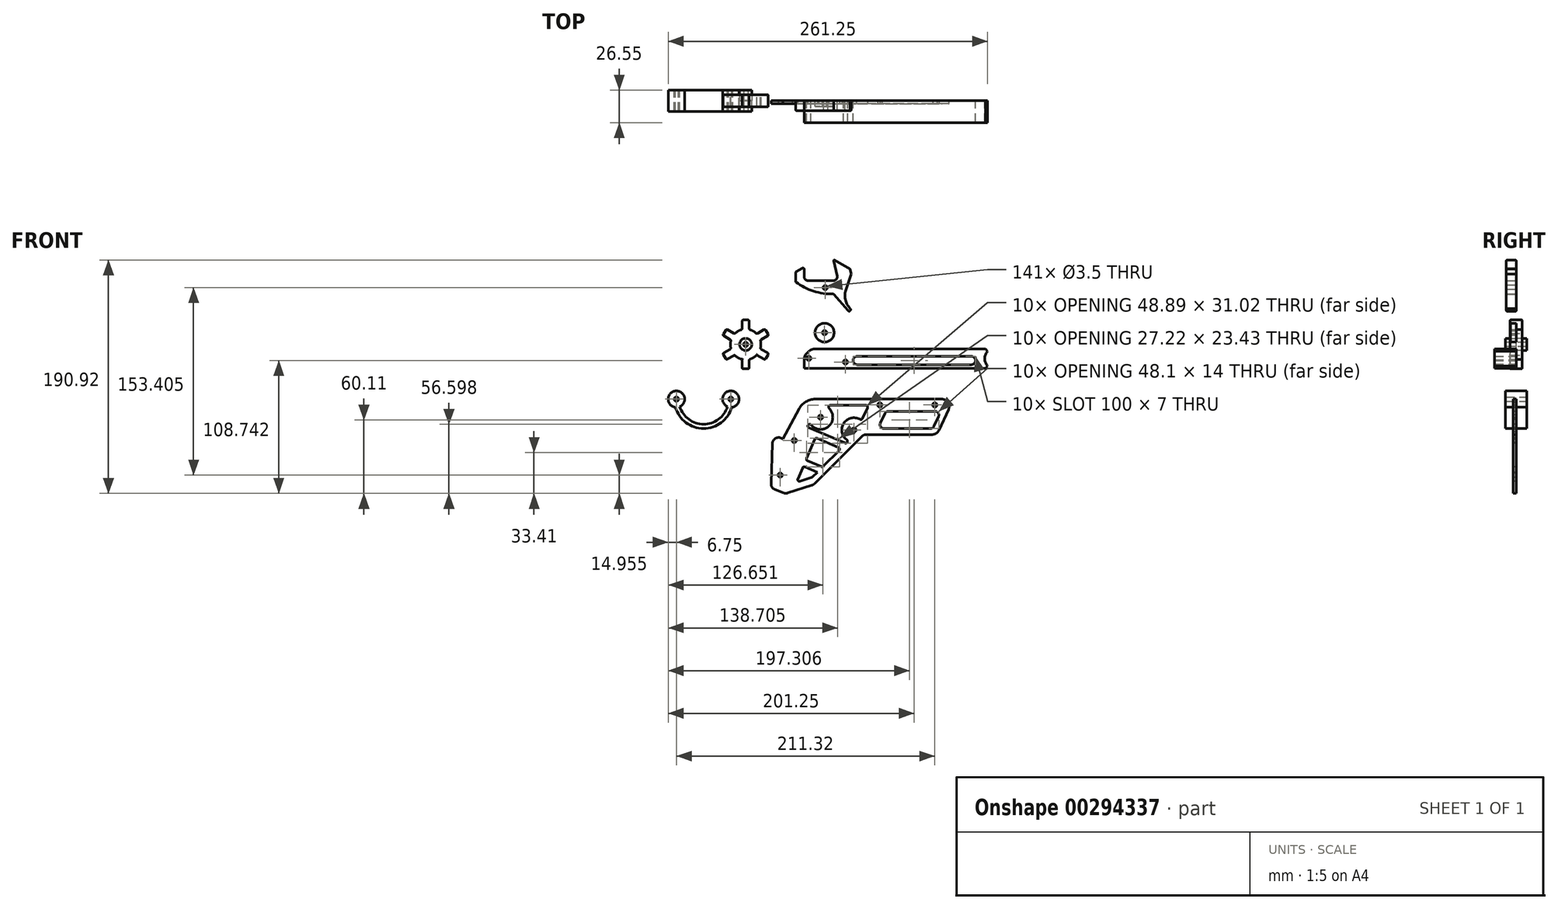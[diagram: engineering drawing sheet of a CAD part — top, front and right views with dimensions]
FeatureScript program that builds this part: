
annotation { "Feature Type Name" : "Feature", "Feature Type Description" : "" }
export const myFeature = defineFeature(function(context is Context, id is Id, definition is map)
    precondition{}
    {
        {
            var Q0;
            Q0=qCreatedBy(makeId("Front.planeOp"),FACE);
            var sketch = newSketch(context, id + "F0", { "sketchPlane" : qUnion([Q0])});
            skLineSegment(sketch, "E0", {"start": v(9.01, 0) * mm, "end": v(112.58, 0) * mm});
            skLineSegment(sketch, "E1", {"start": v(118.02, -8.54) * mm, "end": v(110.1, -25.54) * mm});
            skLineSegment(sketch, "E2", {"start": v(104.65, -29) * mm, "end": v(50.73, -29) * mm});
            skLineSegment(sketch, "E3", {"start": v(-4.23, -7.96) * mm, "end": v(-17.37, -32.67) * mm});
            skPoint(sketch, "E4.visualSharp", {"position": v(0, 0) * mm});
            skArc(sketch, "E4.filletArc", {"start": v(9.01, 0) * mm, "mid": v(1.29, -2.14) * mm, "end": v(-4.23, -7.96) * mm});
            skPoint(sketch, "E5.visualSharp", {"position": v(122, 0) * mm});
            skArc(sketch, "E5.filletArc", {"start": v(118.02, -8.54) * mm, "mid": v(117.64, -2.78) * mm, "end": v(112.58, 0) * mm});
            skPoint(sketch, "E6.visualSharp", {"position": v(108.48, -29) * mm});
            skArc(sketch, "E6.filletArc", {"start": v(104.65, -29) * mm, "mid": v(107.88, -28.06) * mm, "end": v(110.1, -25.54) * mm});
            skLineSegment(sketch, "E7", {"start": v(47.2, -30.46) * mm, "end": v(8.5, -69.16) * mm});
            skLineSegment(sketch, "E8", {"start": v(6.5, -70.38) * mm, "end": v(-13.45, -76.87) * mm});
            skLineSegment(sketch, "E9", {"start": v(-16.87, -76.75) * mm, "end": v(-24, -73.87) * mm});
            skLineSegment(sketch, "E10", {"start": v(-27.11, -69.06) * mm, "end": v(-25.97, -36.24) * mm});
            skCircle(sketch, "E11", {"center": v(-20.97, -36.42) * mm, "radius": 5 * mm});
            skLineSegment(sketch, "E12", {"start": v(-17.37, -32.67) * mm, "end": v(-18.62, -32) * mm});
            skPoint(sketch, "E13.visualSharp", {"position": v(48.65, -29) * mm});
            skArc(sketch, "E13.filletArc", {"start": v(50.73, -29) * mm, "mid": v(48.81, -29.38) * mm, "end": v(47.2, -30.46) * mm});
            skPoint(sketch, "E14.visualSharp", {"position": v(7.64, -70.01) * mm});
            skArc(sketch, "E14.filletArc", {"start": v(6.5, -70.38) * mm, "mid": v(7.57, -69.9) * mm, "end": v(8.5, -69.16) * mm});
            skPoint(sketch, "E15.visualSharp", {"position": v(-15.18, -77.43) * mm});
            skArc(sketch, "E15.filletArc", {"start": v(-16.87, -76.75) * mm, "mid": v(-15.17, -77.1) * mm, "end": v(-13.45, -76.87) * mm});
            skPoint(sketch, "E16.visualSharp", {"position": v(-27.24, -72.56) * mm});
            skArc(sketch, "E16.filletArc", {"start": v(-27.11, -69.06) * mm, "mid": v(-26.31, -71.96) * mm, "end": v(-24, -73.87) * mm});
            skSolve(sketch);
        }
        {
            var Q0;
            Q0=makeQuery(id+"F0.imprint","IMPRINT",FACE,{"disambiguationData":[TD([[makeQuery(id+"F0.imprint","IMPRINT",EDGE,{"derivedFrom":sQuery(id+"F0.wireOp",EDGE,"E0")}),-1.0]])]});
            var Q1;
            {var subQ0=sQuery(id+"F0.wireOp",EDGE,"E11");var subQ1=makeQuery(id+"F0.imprint","INTERSECT",VERTEX,{"derivedFrom":[sQuery(id+"F0.wireOp",EDGE,"E10"),subQ0]});Q1=makeQuery(id+"F0.imprint","IMPRINT",FACE,{"disambiguationData":[TD([[makeQuery(id+"F0.imprint","IMPRINT",EDGE,{"disambiguationData":[TD([[subQ1,1.0]])],"derivedFrom":subQ0}),1.0]])]});}
            extrude(context, id + "F1", {"entities" : qUnion([Q0, Q1]), "depth" : 2.5 * mm});
        }
        {
            var Q0;
            Q0=makeQuery(id+"F1.opExtrude","CAP_FACE",FACE,{"disambiguationData":[OSD([sQuery(id+"F0.wireOp",EDGE,"E0"),sQuery(id+"F0.wireOp",EDGE,"E1"),sQuery(id+"F0.wireOp",EDGE,"E2"),sQuery(id+"F0.wireOp",EDGE,"E3"),sQuery(id+"F0.wireOp",EDGE,"E4.filletArc"),sQuery(id+"F0.wireOp",EDGE,"E5.filletArc"),sQuery(id+"F0.wireOp",EDGE,"E6.filletArc"),sQuery(id+"F0.wireOp",EDGE,"E7"),sQuery(id+"F0.wireOp",EDGE,"E8"),sQuery(id+"F0.wireOp",EDGE,"E9"),sQuery(id+"F0.wireOp",EDGE,"E10"),sQuery(id+"F0.wireOp",EDGE,"E11"),sQuery(id+"F0.wireOp",EDGE,"E12"),sQuery(id+"F0.wireOp",EDGE,"E13.filletArc"),sQuery(id+"F0.wireOp",EDGE,"E14.filletArc"),sQuery(id+"F0.wireOp",EDGE,"E15.filletArc"),sQuery(id+"F0.wireOp",EDGE,"E16.filletArc")])],"isStart":false});
            var sketch = newSketch(context, id + "F2", { "sketchPlane" : qUnion([Q0])});
            skLineSegment(sketch, "E17.0", {"start": v(103.38, -24) * mm, "end": v(65, -24) * mm});
            skLineSegment(sketch, "E17.2", {"start": v(109.83, -14.27) * mm, "end": v(106.1, -22.27) * mm});
            skLineSegment(sketch, "E18.1", {"start": v(68.73, -10) * mm, "end": v(107.11, -10) * mm});
            skLineSegment(sketch, "E19", {"start": v(66.01, -11.73) * mm, "end": v(62.28, -19.73) * mm});
            skPoint(sketch, "E20.visualSharp", {"position": v(111.82, -10) * mm});
            skArc(sketch, "E20.filletArc", {"start": v(109.83, -14.27) * mm, "mid": v(109.64, -11.39) * mm, "end": v(107.11, -10) * mm});
            skPoint(sketch, "E21.visualSharp", {"position": v(105.3, -24) * mm});
            skArc(sketch, "E21.filletArc", {"start": v(103.38, -24) * mm, "mid": v(105, -23.53) * mm, "end": v(106.1, -22.27) * mm});
            skPoint(sketch, "E22.visualSharp", {"position": v(66.82, -10) * mm});
            skArc(sketch, "E22.filletArc", {"start": v(68.73, -10) * mm, "mid": v(67.12, -10.47) * mm, "end": v(66.01, -11.73) * mm});
            skPoint(sketch, "E23.visualSharp", {"position": v(60.3, -24) * mm});
            skArc(sketch, "E23.filletArc", {"start": v(62.28, -19.73) * mm, "mid": v(62.47, -22.61) * mm, "end": v(65, -24) * mm});
            skCircle(sketch, "E24", {"center": v(106.82, -4.75) * mm, "radius": 1.75 * mm});
            skCircle(sketch, "E25", {"center": v(61.82, -4.75) * mm, "radius": 1.75 * mm});
            skCircle(sketch, "E26", {"center": v(40.74, -25.25) * mm, "radius": 1.75 * mm});
            skCircle(sketch, "E27", {"center": v(13.4, -14.75) * mm, "radius": 1.75 * mm});
            skCircle(sketch, "E28", {"center": v(-19.62, -62.15) * mm, "radius": 1.75 * mm});
            skCircle(sketch, "E29", {"center": v(-8.1, -33.85) * mm, "radius": 1.75 * mm});
            skLineSegment(sketch, "E30", {"start": v(21.4, -5) * mm, "end": v(50.4, -5) * mm});
            skCircle(sketch, "E31", {"center": v(50.4, -6.5) * mm, "radius": 1.5 * mm});
            skCircle(sketch, "E32", {"center": v(21.4, -6.5) * mm, "radius": 1.5 * mm});
            skLineSegment(sketch, "E33", {"start": v(-6.47, -68.29) * mm, "end": v(6.51, -64.07) * mm});
            skLineSegment(sketch, "E34", {"start": v(6.51, -64.07) * mm, "end": v(10.76, -59.83) * mm});
            skLineSegment(sketch, "E35", {"start": v(-0.8, -54.92) * mm, "end": v(-6.47, -68.29) * mm});
            skCircle(sketch, "E36", {"center": v(-3.8, -65.85) * mm, "radius": 1.5 * mm});
            skCircle(sketch, "E37", {"center": v(8.12, -60.34) * mm, "radius": 1.5 * mm});
            skCircle(sketch, "E38", {"center": v(5.7, -62.76) * mm, "radius": 1.5 * mm});
            skCircle(sketch, "E39", {"center": v(3.3, -49.14) * mm, "radius": 1.5 * mm});
            skCircle(sketch, "E40", {"center": v(9.93, -33.49) * mm, "radius": 1.5 * mm});
            skCircle(sketch, "E41", {"center": v(27.51, -40.95) * mm, "radius": 1.5 * mm});
            skCircle(sketch, "E42", {"center": v(14.55, -53.91) * mm, "radius": 1.5 * mm});
            skLineSegment(sketch, "E43", {"start": v(26.92, -74.55) * mm, "end": v(36.43, -74.55) * mm});
            skLineSegment(sketch, "E44", {"start": v(-0.8, -54.92) * mm, "end": v(10.76, -59.83) * mm});
            skCircle(sketch, "E45", {"center": v(0, -56.9) * mm, "radius": 1.5 * mm});
            skLineSegment(sketch, "E46", {"start": v(1.32, -49.93) * mm, "end": v(14.9, -55.7) * mm});
            skLineSegment(sketch, "E47", {"start": v(-0.8, -54.92) * mm, "end": v(9.14, -31.52) * mm});
            skLineSegment(sketch, "E48", {"start": v(9.14, -31.52) * mm, "end": v(30.15, -40.44) * mm});
            skLineSegment(sketch, "E49", {"start": v(19.38, -58.28) * mm, "end": v(22.63, -55.02) * mm});
            skLineSegment(sketch, "E50", {"start": v(10.76, -59.83) * mm, "end": v(30.15, -40.44) * mm});
            skCircle(sketch, "E51", {"center": v(13.4, -14.75) * mm, "radius": 10 * mm});
            skCircle(sketch, "E52", {"center": v(40.74, -25.25) * mm, "radius": 10 * mm});
            skCircle(sketch, "E53", {"center": v(4.48, -22.02) * mm, "radius": 1.5 * mm});
            skCircle(sketch, "E54", {"center": v(33.94, -34.52) * mm, "radius": 1.5 * mm});
            skLineSegment(sketch, "E55", {"start": v(3.9, -23.4) * mm, "end": v(33.35, -35.9) * mm});
            skLineSegment(sketch, "E56", {"start": v(30.15, -40.44) * mm, "end": v(35, -35.59) * mm});
            skLineSegment(sketch, "E57", {"start": v(14.9, -55.7) * mm, "end": v(10.76, -59.83) * mm});
            skLineSegment(sketch, "E58", {"start": v(9.14, -31.52) * mm, "end": v(11.26, -26.53) * mm});
            skLineSegment(sketch, "E59", {"start": v(1.87, -56.05) * mm, "end": v(3.99, -51.06) * mm});
            skCircle(sketch, "E60", {"center": v(46.34, -15.2) * mm, "radius": 1.5 * mm});
            skLineSegment(sketch, "E61", {"start": v(47.7, -15.84) * mm, "end": v(51.76, -7.13) * mm});
            skSolve(sketch);
        }
        {
            var Q0;
            {var subQ13=sQuery(id+"F2.wireOp",EDGE,"E30");Q0=makeQuery(id+"F2.imprint","IMPRINT",FACE,{"disambiguationData":[TD([[makeQuery(id+"F2.imprint","IMPRINT",EDGE,{"derivedFrom":subQ13}),-1.0]])]});}
            var Q1;
            {var subQ0=sQuery(id+"F2.wireOp",EDGE,"E53");var subQ1=makeQuery(id+"F2.imprint","INTERSECT",VERTEX,{"derivedFrom":[subQ0,sQuery(id+"F2.wireOp",EDGE,"E55")]});Q1=makeQuery(id+"F2.imprint","IMPRINT",FACE,{"disambiguationData":[TD([[makeQuery(id+"F2.imprint","IMPRINT",EDGE,{"disambiguationData":[TD([[subQ1,1.0]])],"derivedFrom":subQ0}),1.0]])]});}
            var Q2;
            {var subQ0=sQuery(id+"F2.wireOp",EDGE,"E32");var subQ1=makeQuery(id+"F2.imprint","INTERSECT",VERTEX,{"derivedFrom":[sQuery(id+"F2.wireOp",EDGE,"E30"),subQ0]});Q2=makeQuery(id+"F2.imprint","IMPRINT",FACE,{"disambiguationData":[TD([[makeQuery(id+"F2.imprint","IMPRINT",EDGE,{"disambiguationData":[TD([[subQ1,-1.0]])],"derivedFrom":subQ0}),1.0]])]});}
            var Q3;
            {var subQ0=sQuery(id+"F2.wireOp",EDGE,"E31");var subQ1=makeQuery(id+"F2.imprint","INTERSECT",VERTEX,{"derivedFrom":[sQuery(id+"F2.wireOp",EDGE,"E30"),subQ0]});Q3=makeQuery(id+"F2.imprint","IMPRINT",FACE,{"disambiguationData":[TD([[makeQuery(id+"F2.imprint","IMPRINT",EDGE,{"disambiguationData":[TD([[subQ1,-1.0]])],"derivedFrom":subQ0}),1.0]])]});}
            var Q4;
            {var subQ0=sQuery(id+"F2.wireOp",EDGE,"E60");var subQ1=makeQuery(id+"F2.imprint","INTERSECT",VERTEX,{"derivedFrom":[subQ0,sQuery(id+"F2.wireOp",EDGE,"E61")]});Q4=makeQuery(id+"F2.imprint","IMPRINT",FACE,{"disambiguationData":[TD([[makeQuery(id+"F2.imprint","IMPRINT",EDGE,{"disambiguationData":[TD([[subQ1,1.0]])],"derivedFrom":subQ0}),1.0]])]});}
            var Q5;
            Q5=makeQuery(id+"F2.imprint","IMPRINT",FACE,{"disambiguationData":[TD([[makeQuery(id+"F2.imprint","IMPRINT",EDGE,{"derivedFrom":sQuery(id+"F2.wireOp",EDGE,"E17.0")}),-1.0]])]});
            var Q6;
            {var subQ0=sQuery(id+"F2.wireOp",EDGE,"E46");var subQ10=sQuery(id+"F2.wireOp",EDGE,"E39");var subQ11=makeQuery(id+"F2.imprint","INTERSECT",VERTEX,{"derivedFrom":[subQ10,subQ0]});Q6=makeQuery(id+"F2.imprint","IMPRINT",FACE,{"disambiguationData":[TD([[makeQuery(id+"F2.imprint","IMPRINT",EDGE,{"disambiguationData":[TD([[subQ11,-1.0]])],"derivedFrom":subQ10}),-1.0]])]});}
            var Q7;
            {var subQ0=sQuery(id+"F2.wireOp",EDGE,"E40");var subQ1=makeQuery(id+"F2.imprint","INTERSECT",VERTEX,{"derivedFrom":[subQ0,sQuery(id+"F2.wireOp",EDGE,"E47")]});Q7=makeQuery(id+"F2.imprint","IMPRINT",FACE,{"disambiguationData":[TD([[makeQuery(id+"F2.imprint","IMPRINT",EDGE,{"disambiguationData":[TD([[subQ1,1.0]])],"derivedFrom":subQ0}),1.0]])]});}
            var Q8;
            {var subQ0=sQuery(id+"F2.wireOp",EDGE,"E39");var subQ1=makeQuery(id+"F2.imprint","INTERSECT",VERTEX,{"derivedFrom":[subQ0,sQuery(id+"F2.wireOp",EDGE,"E46")]});Q8=makeQuery(id+"F2.imprint","IMPRINT",FACE,{"disambiguationData":[TD([[makeQuery(id+"F2.imprint","IMPRINT",EDGE,{"disambiguationData":[TD([[subQ1,1.0]])],"derivedFrom":subQ0}),1.0]])]});}
            var Q9;
            {var subQ0=sQuery(id+"F2.wireOp",EDGE,"E42");var subQ1=makeQuery(id+"F2.imprint","INTERSECT",VERTEX,{"derivedFrom":[subQ0,sQuery(id+"F2.wireOp",EDGE,"E46")]});Q9=makeQuery(id+"F2.imprint","IMPRINT",FACE,{"disambiguationData":[TD([[makeQuery(id+"F2.imprint","IMPRINT",EDGE,{"disambiguationData":[TD([[subQ1,-1.0]])],"derivedFrom":subQ0}),1.0]])]});}
            var Q10;
            {var subQ0=sQuery(id+"F2.wireOp",EDGE,"E41");var subQ1=makeQuery(id+"F2.imprint","INTERSECT",VERTEX,{"derivedFrom":[subQ0,sQuery(id+"F2.wireOp",EDGE,"E48")]});Q10=makeQuery(id+"F2.imprint","IMPRINT",FACE,{"disambiguationData":[TD([[makeQuery(id+"F2.imprint","IMPRINT",EDGE,{"disambiguationData":[TD([[subQ1,-1.0]])],"derivedFrom":subQ0}),1.0]])]});}
            var Q11;
            {var subQ0=sQuery(id+"F2.wireOp",EDGE,"E36");var subQ1=sQuery(id+"F2.wireOp",EDGE,"E33");var subQ2=makeQuery(id+"F2.imprint","INTERSECT",VERTEX,{"derivedFrom":[subQ1,subQ0]});Q11=makeQuery(id+"F2.imprint","IMPRINT",FACE,{"disambiguationData":[TD([[makeQuery(id+"F2.imprint","IMPRINT",EDGE,{"disambiguationData":[TD([[subQ2,-1.0]])],"derivedFrom":subQ1}),1.0]])]});}
            var Q12;
            {var subQ0=sQuery(id+"F2.wireOp",EDGE,"E38");var subQ1=sQuery(id+"F2.wireOp",EDGE,"E37");var subQ2=makeQuery(id+"F2.imprint","INTERSECT",VERTEX,{"disambiguationData":[OD(0.0)],"derivedFrom":[subQ1,subQ0]});Q12=makeQuery(id+"F2.imprint","IMPRINT",FACE,{"disambiguationData":[TD([[makeQuery(id+"F2.imprint","IMPRINT",EDGE,{"disambiguationData":[TD([[subQ2,1.0]])],"derivedFrom":subQ1}),1.0]])]});}
            var Q13;
            {var subQ0=sQuery(id+"F2.wireOp",EDGE,"E36");var subQ1=makeQuery(id+"F2.imprint","INTERSECT",VERTEX,{"derivedFrom":[sQuery(id+"F2.wireOp",EDGE,"E33"),subQ0]});Q13=makeQuery(id+"F2.imprint","IMPRINT",FACE,{"disambiguationData":[TD([[makeQuery(id+"F2.imprint","IMPRINT",EDGE,{"disambiguationData":[TD([[subQ1,1.0]])],"derivedFrom":subQ0}),1.0]])]});}
            var Q14;
            {var subQ0=sQuery(id+"F2.wireOp",EDGE,"E45");var subQ1=makeQuery(id+"F2.imprint","INTERSECT",VERTEX,{"derivedFrom":[sQuery(id+"F2.wireOp",EDGE,"E35"),subQ0]});Q14=makeQuery(id+"F2.imprint","IMPRINT",FACE,{"disambiguationData":[TD([[makeQuery(id+"F2.imprint","IMPRINT",EDGE,{"disambiguationData":[TD([[subQ1,1.0]])],"derivedFrom":subQ0}),1.0]])]});}
            var Q15;
            {var subQ0=sQuery(id+"F2.wireOp",EDGE,"E38");var subQ1=sQuery(id+"F2.wireOp",EDGE,"E37");var subQ2=makeQuery(id+"F2.imprint","INTERSECT",VERTEX,{"disambiguationData":[OD(0.0)],"derivedFrom":[subQ1,subQ0]});Q15=makeQuery(id+"F2.imprint","IMPRINT",FACE,{"disambiguationData":[TD([[makeQuery(id+"F2.imprint","IMPRINT",EDGE,{"disambiguationData":[TD([[subQ2,-1.0]])],"derivedFrom":subQ1}),1.0]])]});}
            var Q16;
            {var subQ0=sQuery(id+"F2.wireOp",EDGE,"E38");var subQ1=sQuery(id+"F2.wireOp",EDGE,"E37");var subQ2=makeQuery(id+"F2.imprint","INTERSECT",VERTEX,{"disambiguationData":[OD(0.0)],"derivedFrom":[subQ1,subQ0]});Q16=makeQuery(id+"F2.imprint","IMPRINT",FACE,{"disambiguationData":[TD([[makeQuery(id+"F2.imprint","IMPRINT",EDGE,{"disambiguationData":[TD([[subQ2,-1.0]])],"derivedFrom":subQ1}),-1.0]])]});}
            var Q17;
            {var subQ0=sQuery(id+"F2.wireOp",EDGE,"E38");var subQ1=sQuery(id+"F2.wireOp",EDGE,"E34");var subQ2=makeQuery(id+"F2.imprint","INTERSECT",VERTEX,{"derivedFrom":[subQ1,subQ0]});Q17=makeQuery(id+"F2.imprint","IMPRINT",FACE,{"disambiguationData":[TD([[makeQuery(id+"F2.imprint","IMPRINT",EDGE,{"disambiguationData":[TD([[subQ2,-1.0]])],"derivedFrom":subQ1}),1.0]])]});}
            var Q18;
            Q18=makeQuery(id+"F2.imprint","IMPRINT",FACE,{"disambiguationData":[TD([[makeQuery(id+"F2.imprint","IMPRINT",EDGE,{"derivedFrom":sQuery(id+"F2.wireOp",EDGE,"E28")}),1.0]])]});
            var Q19;
            Q19=makeQuery(id+"F2.imprint","IMPRINT",FACE,{"disambiguationData":[TD([[makeQuery(id+"F2.imprint","IMPRINT",EDGE,{"derivedFrom":sQuery(id+"F2.wireOp",EDGE,"E29")}),1.0]])]});
            var Q20;
            {var subQ0=sQuery(id+"F2.wireOp",EDGE,"E54");var subQ1=makeQuery(id+"F2.imprint","INTERSECT",VERTEX,{"derivedFrom":[subQ0,sQuery(id+"F2.wireOp",EDGE,"E55")]});Q20=makeQuery(id+"F2.imprint","IMPRINT",FACE,{"disambiguationData":[TD([[makeQuery(id+"F2.imprint","IMPRINT",EDGE,{"disambiguationData":[TD([[subQ1,1.0]])],"derivedFrom":subQ0}),1.0]])]});}
            var Q21;
            Q21=makeQuery(id+"F2.imprint","IMPRINT",FACE,{"disambiguationData":[TD([[makeQuery(id+"F2.imprint","IMPRINT",EDGE,{"derivedFrom":sQuery(id+"F2.wireOp",EDGE,"E27")}),1.0]])]});
            var Q22;
            Q22=makeQuery(id+"F2.imprint","IMPRINT",FACE,{"disambiguationData":[TD([[makeQuery(id+"F2.imprint","IMPRINT",EDGE,{"derivedFrom":sQuery(id+"F2.wireOp",EDGE,"E26")}),1.0]])]});
            var Q23;
            Q23=makeQuery(id+"F2.imprint","IMPRINT",FACE,{"disambiguationData":[TD([[makeQuery(id+"F2.imprint","IMPRINT",EDGE,{"derivedFrom":sQuery(id+"F2.wireOp",EDGE,"E25")}),1.0]])]});
            var Q24;
            Q24=makeQuery(id+"F2.imprint","IMPRINT",FACE,{"disambiguationData":[TD([[makeQuery(id+"F2.imprint","IMPRINT",EDGE,{"derivedFrom":sQuery(id+"F2.wireOp",EDGE,"E24")}),1.0]])]});
            var Q25;
            {var subQ0=sQuery(id+"F2.wireOp",EDGE,"E38");var subQ1=makeQuery(id+"F2.imprint","INTERSECT",VERTEX,{"derivedFrom":[sQuery(id+"F2.wireOp",EDGE,"E33"),subQ0]});Q25=makeQuery(id+"F2.imprint","IMPRINT",FACE,{"disambiguationData":[TD([[makeQuery(id+"F2.imprint","IMPRINT",EDGE,{"disambiguationData":[TD([[subQ1,-1.0]])],"derivedFrom":subQ0}),1.0]])]});}
            extrude(context, id + "F3", {"entities" : qUnion([Q0, Q1, Q2, Q3, Q4, Q5, Q6, Q7, Q8, Q9, Q10, Q11, Q12, Q13, Q14, Q15, Q16, Q17, Q18, Q19, Q20, Q21, Q22, Q23, Q24, Q25]), "operationType" : NewBodyOperationType.REMOVE, "endBound" : BoundingType.THROUGH_ALL, "oppositeDirection" : true, "depth" : 25 * mm});
        }
        {
            var Q0;
            Q0=qCreatedBy(makeId("Front.planeOp"),FACE);
            var sketch = newSketch(context, id + "F4", { "sketchPlane" : qUnion([Q0])});
            skCircle(sketch, "E62", {"center": v(-47.87, 44.76) * mm, "radius": 12.5 * mm});
            skLineSegment(sketch, "E63", {"start": v(-50.8, 56.91) * mm, "end": v(-50.8, 64.76) * mm});
            skLineSegment(sketch, "E64", {"start": v(-50.8, 64.76) * mm, "end": v(-44.93, 64.76) * mm});
            skLineSegment(sketch, "E65", {"start": v(-44.93, 64.76) * mm, "end": v(-44.93, 56.91) * mm});
            skLineSegment(sketch, "E66", {"start": v(-47.87, 64.76) * mm, "end": v(-47.87, 44.76) * mm});
            skLineSegment(sketch, "E67.1.0", {"start": v(-66.66, 52.22) * mm, "end": v(-63.72, 57.3) * mm});
            skLineSegment(sketch, "E67.1.1", {"start": v(-63.72, 57.3) * mm, "end": v(-56.92, 53.38) * mm});
            skLineSegment(sketch, "E67.1.2", {"start": v(-59.86, 48.3) * mm, "end": v(-66.66, 52.22) * mm});
            skLineSegment(sketch, "E67.2.0", {"start": v(-63.72, 32.22) * mm, "end": v(-66.66, 37.3) * mm});
            skLineSegment(sketch, "E67.2.1", {"start": v(-66.66, 37.3) * mm, "end": v(-59.86, 41.23) * mm});
            skLineSegment(sketch, "E67.2.2", {"start": v(-56.92, 36.14) * mm, "end": v(-63.72, 32.22) * mm});
            skLineSegment(sketch, "E67.3.0", {"start": v(-44.93, 24.76) * mm, "end": v(-50.8, 24.76) * mm});
            skLineSegment(sketch, "E67.3.1", {"start": v(-50.8, 24.76) * mm, "end": v(-50.8, 32.61) * mm});
            skLineSegment(sketch, "E67.3.2", {"start": v(-44.93, 32.61) * mm, "end": v(-44.93, 24.76) * mm});
            skLineSegment(sketch, "E67.4.0", {"start": v(-29.08, 37.3) * mm, "end": v(-32.02, 32.22) * mm});
            skLineSegment(sketch, "E67.4.1", {"start": v(-32.02, 32.22) * mm, "end": v(-38.82, 36.14) * mm});
            skLineSegment(sketch, "E67.4.2", {"start": v(-35.88, 41.23) * mm, "end": v(-29.08, 37.3) * mm});
            skLineSegment(sketch, "E67.5.0", {"start": v(-32.02, 57.3) * mm, "end": v(-29.08, 52.22) * mm});
            skLineSegment(sketch, "E67.5.1", {"start": v(-29.08, 52.22) * mm, "end": v(-35.88, 48.3) * mm});
            skLineSegment(sketch, "E67.5.2", {"start": v(-38.82, 53.38) * mm, "end": v(-32.02, 57.3) * mm});
            skSolve(sketch);
        }
        {
            var Q0;
            Q0 = qSketchRegion(id + "F4", true);
            extrude(context, id + "F5", {"entities" : qUnion([Q0]), "endBound" : BoundingType.SYMMETRIC, "depth" : 10 * mm});
        }
        {
            var Q0;
            Q0=qCreatedBy(makeId("Front.planeOp"),FACE);
            var sketch = newSketch(context, id + "F6", { "sketchPlane" : qUnion([Q0])});
            skCircle(sketch, "E68", {"center": v(-47.87, 44.76) * mm, "radius": 5 * mm});
            skCircle(sketch, "E69", {"center": v(-47.87, 44.76) * mm, "radius": 12.5 * mm});
            skSolve(sketch);
        }
        {
            var Q0;
            Q0=makeQuery(id+"F6.imprint","IMPRINT",FACE,{"disambiguationData":[TD([[makeQuery(id+"F6.imprint","IMPRINT",EDGE,{"derivedFrom":sQuery(id+"F6.wireOp",EDGE,"E68")}),1.0]])]});
            var Q1;
            Q1 = qConstructionFilter(qBodyType(qCreatedBy(id + "F6" ,EDGE), BodyType.WIRE), ConstructionObject.NO);
            extrude(context, id + "F7", {"entities" : qUnion([Q0]), "surfaceEntities" : qUnion([Q1]), "depth" : 8.75 * mm});
        }
        {
            var Q0;
            Q0=makeQuery(id+"F6.imprint","IMPRINT",FACE,{"disambiguationData":[TD([[makeQuery(id+"F6.imprint","IMPRINT",EDGE,{"derivedFrom":sQuery(id+"F6.wireOp",EDGE,"E68")}),1.0]])]});
            extrude(context, id + "F8", {"entities" : qUnion([Q0]), "operationType" : NewBodyOperationType.REMOVE, "endBound" : BoundingType.THROUGH_ALL, "oppositeDirection" : true, "depth" : 25 * mm});
        }
        {
            var Q0;
            Q0=makeQuery(id+"F7.opExtrude","CAP_FACE",FACE,{"disambiguationData":[OSD([sQuery(id+"F6.wireOp",EDGE,"E68")])],"isStart":false});
            var sketch = newSketch(context, id + "F9", { "sketchPlane" : qUnion([Q0])});
            skCircle(sketch, "E70", {"center": v(-47.87, 44.76) * mm, "radius": 1.75 * mm});
            skSolve(sketch);
        }
        {
            var Q0;
            Q0=makeQuery(id+"F9.imprint","IMPRINT",FACE,{"disambiguationData":[TD([[makeQuery(id+"F9.imprint","IMPRINT",EDGE,{"derivedFrom":sQuery(id+"F9.wireOp",EDGE,"E70")}),1.0]])]});
            extrude(context, id + "F10", {"entities" : qUnion([Q0]), "operationType" : NewBodyOperationType.REMOVE, "endBound" : BoundingType.THROUGH_ALL, "oppositeDirection" : true, "depth" : 25 * mm});
        }
        {
            var Q0;
            Q0=makeQuery(id+"F5.opExtrude","SWEPT_EDGE",EDGE,{"disambiguationData":[OSD([sQuery(id+"F4.wireOp",EDGE,"E62"),sQuery(id+"F4.wireOp",EDGE,"E67.5.2")])]});
            var Q1;
            Q1=makeQuery(id+"F5.opExtrude","SWEPT_EDGE",EDGE,{"disambiguationData":[OSD([sQuery(id+"F4.wireOp",EDGE,"E62"),sQuery(id+"F4.wireOp",EDGE,"E65")])]});
            var Q2;
            Q2=makeQuery(id+"F5.opExtrude","SWEPT_EDGE",EDGE,{"disambiguationData":[OSD([sQuery(id+"F4.wireOp",EDGE,"E64"),sQuery(id+"F4.wireOp",EDGE,"E65")])]});
            var Q3;
            Q3=makeQuery(id+"F5.opExtrude","SWEPT_EDGE",EDGE,{"disambiguationData":[OSD([sQuery(id+"F4.wireOp",EDGE,"E63"),sQuery(id+"F4.wireOp",EDGE,"E64")])]});
            var Q4;
            Q4=makeQuery(id+"F5.opExtrude","SWEPT_EDGE",EDGE,{"disambiguationData":[OSD([sQuery(id+"F4.wireOp",EDGE,"E67.5.0"),sQuery(id+"F4.wireOp",EDGE,"E67.5.2")])]});
            var Q5;
            Q5=makeQuery(id+"F5.opExtrude","SWEPT_EDGE",EDGE,{"disambiguationData":[OSD([sQuery(id+"F4.wireOp",EDGE,"E67.5.0"),sQuery(id+"F4.wireOp",EDGE,"E67.5.1")])]});
            var Q6;
            Q6=makeQuery(id+"F5.opExtrude","SWEPT_EDGE",EDGE,{"disambiguationData":[OSD([sQuery(id+"F4.wireOp",EDGE,"E62"),sQuery(id+"F4.wireOp",EDGE,"E67.5.1")])]});
            var Q7;
            Q7=makeQuery(id+"F5.opExtrude","SWEPT_EDGE",EDGE,{"disambiguationData":[OSD([sQuery(id+"F4.wireOp",EDGE,"E62"),sQuery(id+"F4.wireOp",EDGE,"E67.4.2")])]});
            var Q8;
            Q8=makeQuery(id+"F5.opExtrude","SWEPT_EDGE",EDGE,{"disambiguationData":[OSD([sQuery(id+"F4.wireOp",EDGE,"E67.4.0"),sQuery(id+"F4.wireOp",EDGE,"E67.4.2")])]});
            var Q9;
            Q9=makeQuery(id+"F5.opExtrude","SWEPT_EDGE",EDGE,{"disambiguationData":[OSD([sQuery(id+"F4.wireOp",EDGE,"E67.4.0"),sQuery(id+"F4.wireOp",EDGE,"E67.4.1")])]});
            var Q10;
            Q10=makeQuery(id+"F5.opExtrude","SWEPT_EDGE",EDGE,{"disambiguationData":[OSD([sQuery(id+"F4.wireOp",EDGE,"E62"),sQuery(id+"F4.wireOp",EDGE,"E67.3.2")])]});
            var Q11;
            Q11=makeQuery(id+"F5.opExtrude","SWEPT_EDGE",EDGE,{"disambiguationData":[OSD([sQuery(id+"F4.wireOp",EDGE,"E67.3.0"),sQuery(id+"F4.wireOp",EDGE,"E67.3.2")])]});
            var Q12;
            Q12=makeQuery(id+"F5.opExtrude","SWEPT_EDGE",EDGE,{"disambiguationData":[OSD([sQuery(id+"F4.wireOp",EDGE,"E67.3.0"),sQuery(id+"F4.wireOp",EDGE,"E67.3.1")])]});
            var Q13;
            Q13=makeQuery(id+"F5.opExtrude","SWEPT_EDGE",EDGE,{"disambiguationData":[OSD([sQuery(id+"F4.wireOp",EDGE,"E62"),sQuery(id+"F4.wireOp",EDGE,"E67.2.2")])]});
            var Q14;
            Q14=makeQuery(id+"F5.opExtrude","SWEPT_EDGE",EDGE,{"disambiguationData":[OSD([sQuery(id+"F4.wireOp",EDGE,"E67.2.0"),sQuery(id+"F4.wireOp",EDGE,"E67.2.2")])]});
            var Q15;
            Q15=makeQuery(id+"F5.opExtrude","SWEPT_EDGE",EDGE,{"disambiguationData":[OSD([sQuery(id+"F4.wireOp",EDGE,"E67.2.0"),sQuery(id+"F4.wireOp",EDGE,"E67.2.1")])]});
            var Q16;
            Q16=makeQuery(id+"F5.opExtrude","SWEPT_EDGE",EDGE,{"disambiguationData":[OSD([sQuery(id+"F4.wireOp",EDGE,"E62"),sQuery(id+"F4.wireOp",EDGE,"E67.1.2")])]});
            var Q17;
            Q17=makeQuery(id+"F5.opExtrude","SWEPT_EDGE",EDGE,{"disambiguationData":[OSD([sQuery(id+"F4.wireOp",EDGE,"E67.1.0"),sQuery(id+"F4.wireOp",EDGE,"E67.1.2")])]});
            var Q18;
            Q18=makeQuery(id+"F5.opExtrude","SWEPT_EDGE",EDGE,{"disambiguationData":[OSD([sQuery(id+"F4.wireOp",EDGE,"E67.1.0"),sQuery(id+"F4.wireOp",EDGE,"E67.1.1")])]});
            var Q19;
            Q19=makeQuery(id+"F5.opExtrude","SWEPT_EDGE",EDGE,{"disambiguationData":[OSD([sQuery(id+"F4.wireOp",EDGE,"E62"),sQuery(id+"F4.wireOp",EDGE,"E67.1.1")])]});
            var Q20;
            Q20=makeQuery(id+"F5.opExtrude","SWEPT_EDGE",EDGE,{"disambiguationData":[OSD([sQuery(id+"F4.wireOp",EDGE,"E62"),sQuery(id+"F4.wireOp",EDGE,"E63")])]});
            var Q21;
            Q21=makeQuery(id+"F5.opExtrude","SWEPT_EDGE",EDGE,{"disambiguationData":[OSD([sQuery(id+"F4.wireOp",EDGE,"E62"),sQuery(id+"F4.wireOp",EDGE,"E67.2.1")])]});
            fillet(context, id + "F11", {"entities" : qUnion([Q0, Q1, Q2, Q3, Q4, Q5, Q6, Q7, Q8, Q9, Q10, Q11, Q12, Q13, Q14, Q15, Q16, Q17, Q18, Q19, Q20, Q21]), "radius" : 1 * mm, "tangentPropagation" : true, "allowEdgeOverflow" : false});
        }
        {
            var Q0;
            Q0=makeQuery(id+"F5.opExtrude","CAP_FACE",FACE,{"disambiguationData":[OSD([sQuery(id+"F4.wireOp",EDGE,"E62"),sQuery(id+"F4.wireOp",EDGE,"E63"),sQuery(id+"F4.wireOp",EDGE,"E64"),sQuery(id+"F4.wireOp",EDGE,"E65"),sQuery(id+"F4.wireOp",EDGE,"E67.1.0"),sQuery(id+"F4.wireOp",EDGE,"E67.1.1"),sQuery(id+"F4.wireOp",EDGE,"E67.1.2"),sQuery(id+"F4.wireOp",EDGE,"E67.2.0"),sQuery(id+"F4.wireOp",EDGE,"E67.2.1"),sQuery(id+"F4.wireOp",EDGE,"E67.2.2"),sQuery(id+"F4.wireOp",EDGE,"E67.3.0"),sQuery(id+"F4.wireOp",EDGE,"E67.3.1"),sQuery(id+"F4.wireOp",EDGE,"E67.3.2"),sQuery(id+"F4.wireOp",EDGE,"E67.4.0"),sQuery(id+"F4.wireOp",EDGE,"E67.4.1"),sQuery(id+"F4.wireOp",EDGE,"E67.4.2"),sQuery(id+"F4.wireOp",EDGE,"E67.5.0"),sQuery(id+"F4.wireOp",EDGE,"E67.5.1"),sQuery(id+"F4.wireOp",EDGE,"E67.5.2")])],"isStart":false});
            var Q1;
            Q1=makeQuery(id+"F5.opExtrude","CAP_FACE",FACE,{"disambiguationData":[OSD([sQuery(id+"F4.wireOp",EDGE,"E62"),sQuery(id+"F4.wireOp",EDGE,"E63"),sQuery(id+"F4.wireOp",EDGE,"E64"),sQuery(id+"F4.wireOp",EDGE,"E65"),sQuery(id+"F4.wireOp",EDGE,"E67.1.0"),sQuery(id+"F4.wireOp",EDGE,"E67.1.1"),sQuery(id+"F4.wireOp",EDGE,"E67.1.2"),sQuery(id+"F4.wireOp",EDGE,"E67.2.0"),sQuery(id+"F4.wireOp",EDGE,"E67.2.1"),sQuery(id+"F4.wireOp",EDGE,"E67.2.2"),sQuery(id+"F4.wireOp",EDGE,"E67.3.0"),sQuery(id+"F4.wireOp",EDGE,"E67.3.1"),sQuery(id+"F4.wireOp",EDGE,"E67.3.2"),sQuery(id+"F4.wireOp",EDGE,"E67.4.0"),sQuery(id+"F4.wireOp",EDGE,"E67.4.1"),sQuery(id+"F4.wireOp",EDGE,"E67.4.2"),sQuery(id+"F4.wireOp",EDGE,"E67.5.0"),sQuery(id+"F4.wireOp",EDGE,"E67.5.1"),sQuery(id+"F4.wireOp",EDGE,"E67.5.2")])],"isStart":true});
            var Q2;
            Q2=makeQuery(id+"F8.boolean.opBoolean","INTERSECT",EDGE,{"derivedFrom":[makeQuery(id+"F5.opExtrude","CAP_FACE",FACE,{"disambiguationData":[OSD([sQuery(id+"F4.wireOp",EDGE,"E62"),sQuery(id+"F4.wireOp",EDGE,"E63"),sQuery(id+"F4.wireOp",EDGE,"E64"),sQuery(id+"F4.wireOp",EDGE,"E65"),sQuery(id+"F4.wireOp",EDGE,"E67.1.0"),sQuery(id+"F4.wireOp",EDGE,"E67.1.1"),sQuery(id+"F4.wireOp",EDGE,"E67.1.2"),sQuery(id+"F4.wireOp",EDGE,"E67.2.0"),sQuery(id+"F4.wireOp",EDGE,"E67.2.1"),sQuery(id+"F4.wireOp",EDGE,"E67.2.2"),sQuery(id+"F4.wireOp",EDGE,"E67.3.0"),sQuery(id+"F4.wireOp",EDGE,"E67.3.1"),sQuery(id+"F4.wireOp",EDGE,"E67.3.2"),sQuery(id+"F4.wireOp",EDGE,"E67.4.0"),sQuery(id+"F4.wireOp",EDGE,"E67.4.1"),sQuery(id+"F4.wireOp",EDGE,"E67.4.2"),sQuery(id+"F4.wireOp",EDGE,"E67.5.0"),sQuery(id+"F4.wireOp",EDGE,"E67.5.1"),sQuery(id+"F4.wireOp",EDGE,"E67.5.2")])],"isStart":true}),makeQuery(id+"F8.opExtrude","SWEPT_FACE",FACE,{"disambiguationData":[OSD([sQuery(id+"F6.wireOp",EDGE,"E68")])]})]});
            fillet(context, id + "F12", {"entities" : qUnion([Q0, Q1, Q2]), "radius" : 0.5 * mm, "tangentPropagation" : true, "allowEdgeOverflow" : false});
        }
        {
            var Q0;
            Q0=qCreatedBy(makeId("Front.planeOp"),FACE);
            var sketch = newSketch(context, id + "F13", { "sketchPlane" : qUnion([Q0])});
            skCircle(sketch, "E71", {"center": v(16.67, 54.4) * mm, "radius": 7.75 * mm});
            skCircle(sketch, "E72", {"center": v(16.67, 54.4) * mm, "radius": 1.75 * mm});
            skSolve(sketch);
        }
        {
            var Q0;
            Q0 = qSketchRegion(id + "F13", true);
            extrude(context, id + "F14", {"entities" : qUnion([Q0]), "depth" : 4.6 * mm});
        }
        {
            var Q0;
            Q0=qCreatedBy(makeId("Front.planeOp"),FACE);
            var sketch = newSketch(context, id + "F15", { "sketchPlane" : qUnion([Q0])});
            skCircle(sketch, "E73", {"center": v(-104.5, 0) * mm, "radius": 6.75 * mm});
            skCircle(sketch, "E74", {"center": v(-60, 0) * mm, "radius": 6.75 * mm});
            skLineSegment(sketch, "E75", {"start": v(-104.5, 0) * mm, "end": v(-60, 0) * mm});
            skArc(sketch, "E76", {"start": v(-101.8, -6.18) * mm, "mid": v(-82.25, -20.5) * mm, "end": v(-62.7, -6.18) * mm});
            skLineSegment(sketch, "E77", {"start": v(-82.25, 0) * mm, "end": v(-82.25, 48.9) * mm});
            skCircle(sketch, "E78", {"center": v(-60, 0) * mm, "radius": 1.75 * mm});
            skCircle(sketch, "E79", {"center": v(-104.5, 0) * mm, "radius": 1.75 * mm});
            skArc(sketch, "E80.0", {"start": v(-105.3, -6.7) * mm, "mid": v(-82.25, -24) * mm, "end": v(-59.2, -6.7) * mm});
            skSolve(sketch);
        }
        {
            var Q0;
            Q0=makeQuery(id+"F15.imprint","IMPRINT",FACE,{"disambiguationData":[TD([[makeQuery(id+"F15.imprint","IMPRINT",EDGE,{"derivedFrom":sQuery(id+"F15.wireOp",EDGE,"E79")}),-1.0]])]});
            var Q1;
            {var subQ0=sQuery(id+"F15.wireOp",EDGE,"E76");Q1=makeQuery(id+"F15.imprint","IMPRINT",FACE,{"disambiguationData":[TD([[makeQuery(id+"F15.imprint","IMPRINT",EDGE,{"derivedFrom":subQ0}),-1.0]])]});}
            var Q2;
            Q2=makeQuery(id+"F15.imprint","IMPRINT",FACE,{"disambiguationData":[TD([[makeQuery(id+"F15.imprint","IMPRINT",EDGE,{"derivedFrom":sQuery(id+"F15.wireOp",EDGE,"E78")}),-1.0]])]});
            extrude(context, id + "F16", {"entities" : qUnion([Q0, Q1, Q2]), "endBound" : BoundingType.SYMMETRIC, "depth" : 17.5 * mm});
        }
        {
            var Q0;
            Q0=qCreatedBy(makeId("Front.planeOp"),FACE);
            var sketch = newSketch(context, id + "F17", { "sketchPlane" : qUnion([Q0])});
            skCircle(sketch, "E81", {"center": v(3, 100) * mm, "radius": 3 * mm});
            skCircle(sketch, "E82", {"center": v(24, 100) * mm, "radius": 3 * mm});
            skLineSegment(sketch, "E83", {"start": v(3, 97) * mm, "end": v(24, 97) * mm});
            skLineSegment(sketch, "E84", {"start": v(26.92, 100.67) * mm, "end": v(23.77, 114.32) * mm});
            skLineSegment(sketch, "E85", {"start": v(0, 100) * mm, "end": v(0, 108) * mm});
            skLineSegment(sketch, "E86", {"start": v(0, 108) * mm, "end": v(-7, 103.96) * mm});
            skCircle(sketch, "E87", {"center": v(-1, 106.27) * mm, "radius": 1 * mm});
            skLineSegment(sketch, "E88", {"start": v(23.77, 114.32) * mm, "end": v(37.63, 106.32) * mm});
            skLineSegment(sketch, "E89", {"start": v(38.32, 102.38) * mm, "end": v(34.3, 90.01) * mm});
            skArc(sketch, "E90", {"start": v(34.3, 90.01) * mm, "mid": v(33.64, 81.53) * mm, "end": v(37.7, 74.06) * mm});
            skCircle(sketch, "E91", {"center": v(36.75, 73.24) * mm, "radius": 1.25 * mm});
            skLineSegment(sketch, "E92", {"start": v(35.8, 72.42) * mm, "end": v(24, 86) * mm});
            skLineSegment(sketch, "E93", {"start": v(-7, 103.96) * mm, "end": v(-7, 95.96) * mm});
            skLineSegment(sketch, "E94", {"start": v(35.8, 72.42) * mm, "end": v(37.7, 74.06) * mm});
            skLineSegment(sketch, "E95", {"start": v(37.63, 106.32) * mm, "end": v(38.32, 102.38) * mm});
            skArc(sketch, "E96", {"start": v(-7, 95.96) * mm, "mid": v(7.67, 88.39) * mm, "end": v(24, 86) * mm});
            skSolve(sketch);
        }
        {
            var Q0;
            Q0=makeQuery(id+"F17.imprint","IMPRINT",FACE,{"disambiguationData":[TD([[makeQuery(id+"F17.imprint","IMPRINT",EDGE,{"derivedFrom":sQuery(id+"F17.wireOp",EDGE,"tVsSgCqr-rb9H-eazK-XmY3-G6WqcgKZKgJh")}),1.0]])]});
            var Q1;
            {var subQ0=sQuery(id+"F17.wireOp",EDGE,"E91");var subQ1=sQuery(id+"F17.wireOp",EDGE,"E90");var subQ3=makeQuery(id+"F17.imprint","INTERSECT",VERTEX,{"derivedFrom":[subQ1,subQ0]});Q1=makeQuery(id+"F17.imprint","IMPRINT",FACE,{"disambiguationData":[TD([[makeQuery(id+"F17.imprint","IMPRINT",EDGE,{"disambiguationData":[TD([[subQ3,-1.0]])],"derivedFrom":subQ1}),1.0]])]});}
            var Q2;
            {var subQ0=sQuery(id+"F17.wireOp",EDGE,"E94");Q2=makeQuery(id+"F17.imprint","IMPRINT",FACE,{"disambiguationData":[TD([[makeQuery(id+"F17.imprint","IMPRINT",EDGE,{"derivedFrom":subQ0}),-1.0]])]});}
            var Q3;
            {var subQ0=sQuery(id+"F17.wireOp",EDGE,"E87");var subQ1=makeQuery(id+"F17.imprint","INTERSECT",VERTEX,{"derivedFrom":[sQuery(id+"F17.wireOp",EDGE,"E85"),subQ0]});Q3=makeQuery(id+"F17.imprint","IMPRINT",FACE,{"disambiguationData":[TD([[makeQuery(id+"F17.imprint","IMPRINT",EDGE,{"disambiguationData":[TD([[subQ1,-1.0]])],"derivedFrom":subQ0}),1.0]])]});}
            var Q4;
            {var subQ0=sQuery(id+"F17.wireOp",EDGE,"E94");Q4=makeQuery(id+"F17.imprint","IMPRINT",FACE,{"disambiguationData":[TD([[makeQuery(id+"F17.imprint","IMPRINT",EDGE,{"derivedFrom":subQ0}),1.0]])]});}
            var Q5;
            {var subQ9=sQuery(id+"F17.wireOp",EDGE,"E83");Q5=makeQuery(id+"F17.imprint","IMPRINT",FACE,{"disambiguationData":[TD([[makeQuery(id+"F17.imprint","IMPRINT",EDGE,{"derivedFrom":subQ9}),-1.0]])]});}
            extrude(context, id + "F18", {"entities" : qUnion([Q0, Q1, Q2, Q3, Q4, Q5]), "depth" : 8 * mm});
        }
        {
            var Q0;
            Q0=makeQuery(id+"F18.opExtrude","SWEPT_EDGE",EDGE,{"disambiguationData":[OSD([sQuery(id+"F17.wireOp",EDGE,"E84"),sQuery(id+"F17.wireOp",EDGE,"E88")])]});
            var Q1;
            Q1=makeQuery(id+"F18.opExtrude","SWEPT_EDGE",EDGE,{"disambiguationData":[OSD([sQuery(id+"F17.wireOp",EDGE,"E86"),sQuery(id+"F17.wireOp",EDGE,"E93")])]});
            var Q2;
            Q2=makeQuery(id+"F18.opExtrude","SWEPT_EDGE",EDGE,{"disambiguationData":[OSD([sQuery(id+"F17.wireOp",EDGE,"E93"),sQuery(id+"F17.wireOp",EDGE,"E96")])]});
            var Q3;
            Q3=makeQuery(id+"F18.opExtrude","SWEPT_EDGE",EDGE,{"disambiguationData":[OSD([sQuery(id+"F17.wireOp",EDGE,"E92"),sQuery(id+"F17.wireOp",EDGE,"E96")])]});
            var Q4;
            Q4=makeQuery(id+"F18.opExtrude","SWEPT_EDGE",EDGE,{"disambiguationData":[OSD([sQuery(id+"F17.wireOp",EDGE,"E89"),sQuery(id+"F17.wireOp",EDGE,"E90")])]});
            var Q5;
            Q5=makeQuery(id+"F18.opExtrude","CAP_FACE",FACE,{"disambiguationData":[OSD([sQuery(id+"F17.wireOp",EDGE,"E81"),sQuery(id+"F17.wireOp",EDGE,"E82"),sQuery(id+"F17.wireOp",EDGE,"E83"),sQuery(id+"F17.wireOp",EDGE,"E84"),sQuery(id+"F17.wireOp",EDGE,"E85"),sQuery(id+"F17.wireOp",EDGE,"E86"),sQuery(id+"F17.wireOp",EDGE,"E87"),sQuery(id+"F17.wireOp",EDGE,"E88"),sQuery(id+"F17.wireOp",EDGE,"E89"),sQuery(id+"F17.wireOp",EDGE,"E90"),sQuery(id+"F17.wireOp",EDGE,"E91"),sQuery(id+"F17.wireOp",EDGE,"E92"),sQuery(id+"F17.wireOp",EDGE,"E93"),sQuery(id+"F17.wireOp",EDGE,"E95"),sQuery(id+"F17.wireOp",EDGE,"E96")])],"isStart":false});
            var Q6;
            Q6=makeQuery(id+"F18.opExtrude","CAP_FACE",FACE,{"disambiguationData":[OSD([sQuery(id+"F17.wireOp",EDGE,"E81"),sQuery(id+"F17.wireOp",EDGE,"E82"),sQuery(id+"F17.wireOp",EDGE,"E83"),sQuery(id+"F17.wireOp",EDGE,"E84"),sQuery(id+"F17.wireOp",EDGE,"E85"),sQuery(id+"F17.wireOp",EDGE,"E86"),sQuery(id+"F17.wireOp",EDGE,"E87"),sQuery(id+"F17.wireOp",EDGE,"E88"),sQuery(id+"F17.wireOp",EDGE,"E89"),sQuery(id+"F17.wireOp",EDGE,"E90"),sQuery(id+"F17.wireOp",EDGE,"E91"),sQuery(id+"F17.wireOp",EDGE,"E92"),sQuery(id+"F17.wireOp",EDGE,"E93"),sQuery(id+"F17.wireOp",EDGE,"E95"),sQuery(id+"F17.wireOp",EDGE,"E96")])],"isStart":true});
            fillet(context, id + "F19", {"entities" : qUnion([Q0, Q1, Q2, Q3, Q4, Q5, Q6]), "radius" : 0.5 * mm, "tangentPropagation" : true, "allowEdgeOverflow" : false});
        }
        {
            var Q0;
            Q0=qCreatedBy(makeId("Front.planeOp"),FACE);
            var sketch = newSketch(context, id + "F20", { "sketchPlane" : qUnion([Q0])});
            skLineSegment(sketch, "E97", {"start": v(9.5, 41.13) * mm, "end": v(148.4, 41.13) * mm});
            skLineSegment(sketch, "E98", {"start": v(0, 25.13) * mm, "end": v(148.4, 25.13) * mm});
            skLineSegment(sketch, "E99", {"start": v(148.4, 41.13) * mm, "end": v(150, 39.22) * mm});
            skLineSegment(sketch, "E100", {"start": v(148.4, 25.13) * mm, "end": v(150, 27.05) * mm});
            skArc(sketch, "E101", {"start": v(150, 39.22) * mm, "mid": v(147.63, 33.13) * mm, "end": v(150, 27.05) * mm});
            skCircle(sketch, "E102", {"center": v(9.5, 31.63) * mm, "radius": 9.5 * mm});
            skLineSegment(sketch, "E103", {"start": v(0, 31.63) * mm, "end": v(0, 25.13) * mm});
            skLineSegment(sketch, "E104", {"start": v(43.5, 31.63) * mm, "end": v(136.5, 31.63) * mm});
            skArc(sketch, "E105.0.startCap", {"start": v(43.5, 28.13) * mm, "mid": v(40, 31.63) * mm, "end": v(43.5, 35.13) * mm});
            skArc(sketch, "E105.0.endCap", {"start": v(136.5, 35.13) * mm, "mid": v(140, 31.63) * mm, "end": v(136.5, 28.13) * mm});
            skLineSegment(sketch, "E105.0.left", {"start": v(43.5, 35.13) * mm, "end": v(136.5, 35.13) * mm});
            skLineSegment(sketch, "E105.0.right", {"start": v(43.5, 28.13) * mm, "end": v(136.5, 28.13) * mm});
            skCircle(sketch, "E106", {"center": v(33.75, 30.38) * mm, "radius": 1.75 * mm});
            skCircle(sketch, "E107", {"center": v(3.75, 33.38) * mm, "radius": 1.75 * mm});
            skSolve(sketch);
        }
        {
            var Q0;
            {var subQ0=sQuery(id+"F20.wireOp",EDGE,"E103");Q0=makeQuery(id+"F20.imprint","IMPRINT",FACE,{"disambiguationData":[TD([[makeQuery(id+"F20.imprint","IMPRINT",EDGE,{"derivedFrom":subQ0}),1.0]])]});}
            var Q1;
            {var subQ1=sQuery(id+"F20.wireOp",EDGE,"E97");Q1=makeQuery(id+"F20.imprint","IMPRINT",FACE,{"disambiguationData":[TD([[makeQuery(id+"F20.imprint","IMPRINT",EDGE,{"derivedFrom":subQ1}),-1.0]])]});}
            var Q2;
            Q2=makeQuery(id+"F20.imprint","IMPRINT",FACE,{"disambiguationData":[TD([[makeQuery(id+"F20.imprint","IMPRINT",EDGE,{"derivedFrom":sQuery(id+"F20.wireOp",EDGE,"E107")}),-1.0]])]});
            extrude(context, id + "F21", {"entities" : qUnion([Q0, Q1, Q2]), "depth" : 17.8 * mm});
        }
        {
            var Q0;
            Q0=makeQuery(id+"F18.opExtrude","CAP_FACE",FACE,{"disambiguationData":[OSD([sQuery(id+"F17.wireOp",EDGE,"E81"),sQuery(id+"F17.wireOp",EDGE,"E82"),sQuery(id+"F17.wireOp",EDGE,"E83"),sQuery(id+"F17.wireOp",EDGE,"E84"),sQuery(id+"F17.wireOp",EDGE,"E85"),sQuery(id+"F17.wireOp",EDGE,"E86"),sQuery(id+"F17.wireOp",EDGE,"E87"),sQuery(id+"F17.wireOp",EDGE,"E88"),sQuery(id+"F17.wireOp",EDGE,"E89"),sQuery(id+"F17.wireOp",EDGE,"E90"),sQuery(id+"F17.wireOp",EDGE,"E91"),sQuery(id+"F17.wireOp",EDGE,"E92"),sQuery(id+"F17.wireOp",EDGE,"E93"),sQuery(id+"F17.wireOp",EDGE,"E95"),sQuery(id+"F17.wireOp",EDGE,"E96")])],"isStart":false});
            var sketch = newSketch(context, id + "F22", { "sketchPlane" : qUnion([Q0])});
            skCircle(sketch, "E108", {"center": v(17.25, 91.25) * mm, "radius": 1.75 * mm});
            skSolve(sketch);
        }
        {
            var Q0;
            Q0 = qSketchRegion(id + "F22", true);
            extrude(context, id + "F23", {"entities" : qUnion([Q0]), "operationType" : NewBodyOperationType.REMOVE, "endBound" : BoundingType.THROUGH_ALL, "oppositeDirection" : true, "depth" : 25 * mm});
        }
        {
            var Q0;
            Q0=makeQuery(id+"F8.boolean.opBoolean","COPY",FACE,{"derivedFrom":makeQuery(id+"F8.opExtrude","CAP_FACE",FACE,{"disambiguationData":[OSD([sQuery(id+"F6.wireOp",EDGE,"E68")])],"isStart":true})});
            extrude(context, id + "F24", {"entities" : qUnion([Q0]), "depth" : 8.75 * mm});
        }
    });
